# Revit family: Lighting_Outside_Nordlux_Arki
name_source: partatom
category: Lighting Fixtures
revit_build: Autodesk Revit 2017 (Build: 20160225_1515(x64)
units: mm (PartAtom-declared; Revit-internal decimal feet)

## family parameters
Cut with Voids When Loaded = No
Host = Face
Light Source = Yes
OmniClass Number = 23.80.70.00
OmniClass Title = Lighting
Part Type = Normal
Room Calculation Point = No
Round Connector Dimension = Use Diameter
Shared = No

## types (2) — shared parameters
AssetType = Fixed
BIMObjectName = Lighting_Outside_Nordlux_Arki
Brand = Nordlux
Category = Outdoor lighting
Collection = Arki
Color Filter = 16777215
ConvergoRefNr = 0143-1909-0042-DK
Description = ARKI OUTDOOR is inspired by the shade of a classical architect light. It expresses simplicity and timelessness, and is therefore complementary to many different styles. Design by Bønnelycke MDD.
Designer = Bonnelycke MDD
Dimming Lamp Color Temperature Shift = <None>
DurationUnit = Hours
Emit Shape Visible in Rendering = No
Emit from Circle Diameter = 50 mm  [stored 0.164042 ft]
EnergyClass = A++ - B
Features = Parallel connection possible
Finish = Galvanized steel, plastic
HasProtectiveEarth = No
IP_Code = IP54
IfcExportAs = IfcLightFixtureType
IfcExportType = NOTDEFINED
InsulationStandardClass = Class 1 (Earth contact)
LensMaterial = Opal white
LightFixtureMountingType = Surface
LightFixturePlacingType = Wall
LightSource = Not included
Manufacturer = Nordlux
ManufacturerName = Nordlux
ManufacturerURL = https://www.nordlux.com
Material = Metal
NBSDescription = General purpose luminaires
NBSReference = 90-60-50/405
Name = Nordlux_Arki
NominalCurrent = 0 A
NominalDiameter = 200 mm  [stored 0.656168 ft]
NominalFrequencyRange = 50 Hz
NominalHeight = 262 mm
NominalLength = 202 mm  [stored 0.66273 ft]
NominalRadius = 100 mm  [stored 0.328084 ft]
NominalVoltage = 230 V
NominalVoltageCalc = 0 V
NominalWidth = 204 mm
NumberOfPoles = 1
PhaseAngle = 0.00°
Photometric Web File = 7518 Arki Outdoor Væg Sort.ies
Product data url = https://www.bimobject.com
ProductInformation = ARKI OUTDOOR is inspired by the shade of a classical architect light. It expresses simplicity and timelessness, and is therefore complementary to many different styles. Design by Bønnelycke MDD.
Shape = Sculptured
Size = 200x260x200mm
Socket = E27
Tilt Angle = 90.00°
TotalWattage = 20 W
URL = https://www.nordlux.com
Uniclass2 = Pr_70_70_48_85
Uniclass2015Description = Surface luminaires
Uniclass2015Reference = Pr_70_70_48_85
UsageCurrent = 0 A
Version = 1
VersionDate = 30/08/2019
WarrantyDurationUnit = Hours
zero-valued in all types: Default Elevation, ElectricalDeviceNominalPower, MaintenanceFactor, NumberOfSources

## per-type parameters (varying)
| type | ArticleNumber | Color | EANNumber | LightFixtureMainMaterial | ModelReference |
| Arki - black | 75181003 | Black | 5701581280175 | Black | 75181003 |
| Arki - brushed steel | 75181031 | Grey | 5701581280274 | Brushed steel | 75181031 |

note: column(s) folded — value = type name in every type: Model

note: [stored X ft] marks values corroborated as IEEE doubles in the binary element streams (Revit-internal decimal feet)

## geometry (parser evidence)
native form markers: Sweep x6
no freeform markers — native parametric forms only
